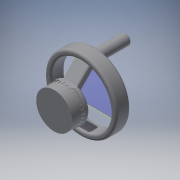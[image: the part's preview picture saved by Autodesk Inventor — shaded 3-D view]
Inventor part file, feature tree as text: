
AUTODESK INVENTOR PART (.ipt)
format: ipt  version: 2016 (Build 200138000, 138)  size: 551,936 bytes
history: native  units: mm
features: extrude x13, sketch x13, fillet x6, pattern_circular x1, chamfer x1, plane x1
ambient origin geometry x8: Origin, YZ Plane, XZ Plane, XY Plane, X Axis, Y Axis, Z Axis, Center Point
bodies: Solid1 (feature_tree)
feature tree (35):
  extrude  "Extrusion1"  Depth=20.0mm TaperAngle=0.0deg
  extrude  "Extrusion2"  Depth=5.0mm TaperAngle=0.0deg
  extrude  "Extrusion3"  Depth=5.0mm
  pattern_circular  "Circular Pattern1"  Count=30 Angle=360.0deg
  extrude  "Extrusion4"  Depth=10.0mm TaperAngle=0.0deg
  extrude  "Extrusion5"  Depth=16.0mm
  extrude  "Extrusion6"  Depth=10.0mm
  chamfer  "Chamfer1"  Distance=10.0mm
  plane  "Work Plane1"
  extrude  "Extrusion7"  Depth=2.0mm
  fillet  "Fillet1"  Radius=150.0mm
  extrude  "Extrusion8"  Depth=5.0mm TaperAngle=0.0deg
  fillet  "Fillet2"  Radius=5.0mm
  extrude  "Extrusion9"  Depth=5.0mm
  fillet  "Fillet3"  Radius=62.25mm
  extrude  "Extrusion10"  Depth=5.0mm TaperAngle=0.0deg
  fillet  "Fillet4"  Radius=4.0mm
  extrude  "Extrusion11"  Depth=4.0mm
  fillet  "Fillet5"  Radius=22.0mm
  extrude  "Extrusion12"  Depth=2.0mm TaperAngle=0.0deg
  extrude  "Extrusion13"  Depth=2.0mm
  fillet  "Fillet6"  [1 undecoded]
  sketch  "Sketch1"  dims[d0=75.0mm d1=20.0mm d2=0.0mm]
  sketch  "Sketch2"  dims[d3=76.0mm d4=5.0mm d5=0.0mm]
  sketch  "Sketch3"  dims[d7=2.5mm d8=5.0mm]
  sketch  "Sketch4"  dims[d9=5.0mm d10=0.0mm d11=300.0mm d12=360.0deg]
  sketch  "Sketch5"  dims[d14=78.0mm d15=10.0mm d16=0.0mm]
  sketch  "Sketch6"  dims[d17=16.0mm d18=16.0mm]
  sketch  "Sketch7"  dims[d19=10.0mm d20=0.0mm d21=55.0mm d22=10.0mm d23=0.0mm]
  sketch  "Sketch8"  dims[d24=10.0mm d25=2.0mm d26=45.0deg d27=50.0mm d28=150.0mm]
  sketch  "Sketch9"  dims[d29=125.0mm d30=30.0mm d31=0.0mm d32=5.0mm]
  sketch  "Sketch10"  dims[d33=61.75mm d34=0.0mm d35=5.0mm d36=62.25mm d37=0.0mm]
  sketch  "Sketch11"  dims[d38=5.0mm d39=32.0mm d40=0.0mm d41=4.0mm]
  sketch  "Sketch12"  dims[d42=32.0mm d43=0.0mm d44=4.0mm d45=22.0mm]
  sketch  "Sketch13"  dims[d46=50.0mm d47=0.0mm d48=40.0mm d49=0.0mm d50=2.0mm]
note: 1 required parameter value undecoded (feature->parameter linkage not recoverable at this tier; creation-order binding heuristic only, values carry confidence <= 0.55)
